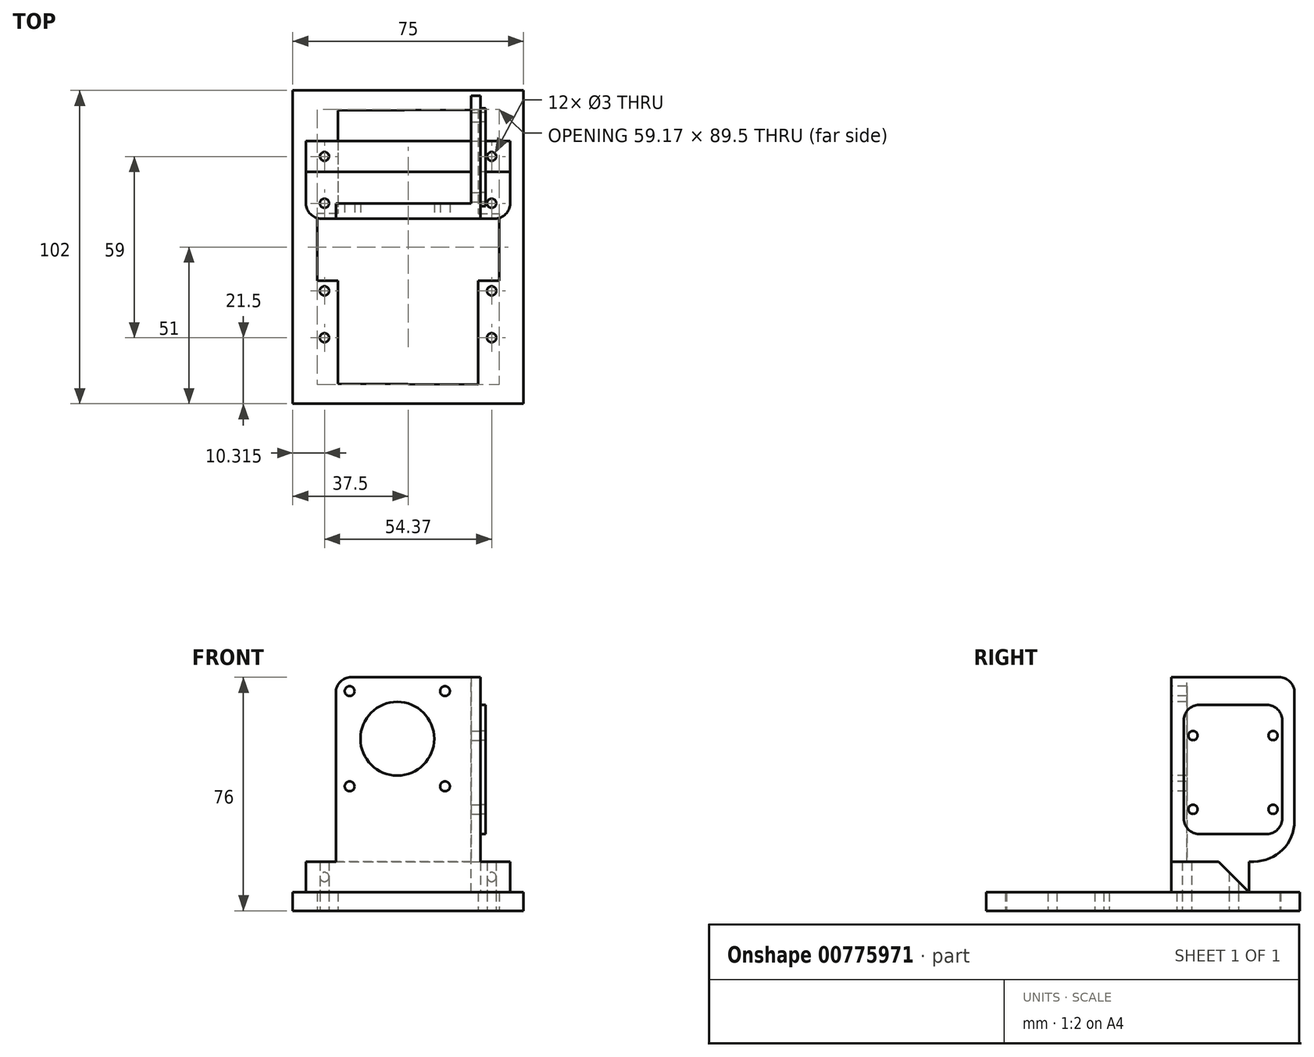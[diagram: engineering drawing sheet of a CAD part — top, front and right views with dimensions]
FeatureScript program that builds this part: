
annotation { "Feature Type Name" : "Feature", "Feature Type Description" : "" }
export const myFeature = defineFeature(function(context is Context, id is Id, definition is map)
    precondition{}
    {
        {
            var Q0;
            Q0=qCreatedBy(makeId("Top.planeOp"),FACE);
            var sketch = newSketch(context, id + "F0", { "sketchPlane" : qUnion([Q0])});
            skLineSegment(sketch, "E0.bottom", {"start": v(-22.79, 44.45) * mm, "end": v(22.79, 44.75) * mm});
            skPoint(sketch, "E0.middle", {"position": v(0, 0) * mm});
            skCircle(sketch, "E1", {"center": v(27.18, 29.5) * mm, "radius": 1.5 * mm});
            skCircle(sketch, "E2", {"center": v(27.18, 14.25) * mm, "radius": 1.5 * mm});
            skLineSegment(sketch, "E3", {"start": v(0, 44.6) * mm, "end": v(0, -44.6) * mm, "construction": true});
            skLineSegment(sketch, "E4", {"start": v(29.59, 0) * mm, "end": v(-29.59, 0) * mm, "construction": true});
            skLineSegment(sketch, "E5", {"start": v(27.18, 29.5) * mm, "end": v(27.18, 14.25) * mm});
            skCircle(sketch, "E6.MirrorC", {"center": v(-27.18, 29.5) * mm, "radius": 1.5 * mm});
            skCircle(sketch, "E7.MirrorC", {"center": v(-27.18, 14.25) * mm, "radius": 1.5 * mm});
            skCircle(sketch, "E8.MirrorC", {"center": v(-27.18, -14.25) * mm, "radius": 1.5 * mm});
            skCircle(sketch, "E9.MirrorC", {"center": v(-27.18, -29.5) * mm, "radius": 1.5 * mm});
            skCircle(sketch, "E10.MirrorC", {"center": v(27.18, -14.25) * mm, "radius": 1.5 * mm});
            skCircle(sketch, "E11.MirrorC", {"center": v(27.19, -29.5) * mm, "radius": 1.5 * mm});
            skLineSegment(sketch, "E12", {"start": v(22.78, 44.75) * mm, "end": v(22.78, 10.95) * mm});
            skLineSegment(sketch, "E13", {"start": v(22.79, 10.95) * mm, "end": v(29.59, 10.95) * mm});
            skLineSegment(sketch, "E14", {"start": v(-22.79, 44.45) * mm, "end": v(-22.79, 10.95) * mm});
            skLineSegment(sketch, "E15", {"start": v(-22.78, 10.95) * mm, "end": v(-29.58, 10.95) * mm});
            skLineSegment(sketch, "E16", {"start": v(-29.59, 10.95) * mm, "end": v(-29.59, 0) * mm});
            skLineSegment(sketch, "E17", {"start": v(29.59, 10.95) * mm, "end": v(29.59, 0) * mm});
            skLineSegment(sketch, "E18.MirrorCS", {"start": v(-29.59, -10.95) * mm, "end": v(-29.59, 0) * mm});
            skLineSegment(sketch, "E19.MirrorCS", {"start": v(-22.78, -10.95) * mm, "end": v(-29.58, -10.95) * mm});
            skLineSegment(sketch, "E20.MirrorCS", {"start": v(-22.78, -44.45) * mm, "end": v(-22.79, -10.95) * mm});
            skLineSegment(sketch, "E21.MirrorCS", {"start": v(22.79, -44.75) * mm, "end": v(22.79, -10.95) * mm});
            skLineSegment(sketch, "E22.MirrorCS", {"start": v(22.79, -10.95) * mm, "end": v(29.59, -10.95) * mm});
            skLineSegment(sketch, "E23.MirrorCS", {"start": v(29.59, -10.95) * mm, "end": v(29.59, 0) * mm});
            skLineSegment(sketch, "E24.MirrorCS", {"start": v(-22.79, -44.45) * mm, "end": v(22.79, -44.75) * mm});
            skLineSegment(sketch, "E25.bottom", {"start": v(37.5, 51) * mm, "end": v(-37.5, 51) * mm});
            skLineSegment(sketch, "E25.top", {"start": v(37.5, -51) * mm, "end": v(-37.5, -51) * mm});
            skLineSegment(sketch, "E25.left", {"start": v(37.5, 51) * mm, "end": v(37.5, -51) * mm});
            skLineSegment(sketch, "E25.right", {"start": v(-37.5, 51) * mm, "end": v(-37.5, -51) * mm});
            skSolve(sketch);
        }
        {
            var Q0;
            Q0=makeQuery(id+"F0.imprint","IMPRINT",FACE,{"disambiguationData":[TD([[makeQuery(id+"F0.imprint","IMPRINT",EDGE,{"derivedFrom":sQuery(id+"F0.wireOp",EDGE,"E0.bottom")}),1.0]])]});
            extrude(context, id + "F1", {"entities" : qUnion([Q0]), "depth" : 6 * mm, "offsetDistance" : 25 * mm});
        }
        {
            var Q0;
            Q0=makeQuery(id+"F1.opExtrude","CAP_FACE",FACE,{"disambiguationData":[OSD([sQuery(id+"F0.wireOp",EDGE,"E0.bottom"),sQuery(id+"F0.wireOp",EDGE,"E1"),sQuery(id+"F0.wireOp",EDGE,"E2"),sQuery(id+"F0.wireOp",EDGE,"E6.MirrorC"),sQuery(id+"F0.wireOp",EDGE,"E7.MirrorC"),sQuery(id+"F0.wireOp",EDGE,"E8.MirrorC"),sQuery(id+"F0.wireOp",EDGE,"E9.MirrorC"),sQuery(id+"F0.wireOp",EDGE,"E10.MirrorC"),sQuery(id+"F0.wireOp",EDGE,"E11.MirrorC"),sQuery(id+"F0.wireOp",EDGE,"E12"),sQuery(id+"F0.wireOp",EDGE,"E13"),sQuery(id+"F0.wireOp",EDGE,"E14"),sQuery(id+"F0.wireOp",EDGE,"E15"),sQuery(id+"F0.wireOp",EDGE,"E16"),sQuery(id+"F0.wireOp",EDGE,"E17"),sQuery(id+"F0.wireOp",EDGE,"E18.MirrorCS"),sQuery(id+"F0.wireOp",EDGE,"E19.MirrorCS"),sQuery(id+"F0.wireOp",EDGE,"E20.MirrorCS"),sQuery(id+"F0.wireOp",EDGE,"E21.MirrorCS"),sQuery(id+"F0.wireOp",EDGE,"E22.MirrorCS"),sQuery(id+"F0.wireOp",EDGE,"E23.MirrorCS"),sQuery(id+"F0.wireOp",EDGE,"E24.MirrorCS"),sQuery(id+"F0.wireOp",EDGE,"E25.bottom"),sQuery(id+"F0.wireOp",EDGE,"E25.top"),sQuery(id+"F0.wireOp",EDGE,"E25.left"),sQuery(id+"F0.wireOp",EDGE,"E25.right")])],"isStart":false});
            var sketch = newSketch(context, id + "F2", { "sketchPlane" : qUnion([Q0])});
            skLineSegment(sketch, "E26.bottom", {"start": v(-33.18, 34.5) * mm, "end": v(33.18, 34.5) * mm});
            skLineSegment(sketch, "E26.top", {"start": v(-33.18, 9.25) * mm, "end": v(33.18, 9.25) * mm});
            skLineSegment(sketch, "E26.left", {"start": v(-33.18, 34.5) * mm, "end": v(-33.18, 9.25) * mm});
            skLineSegment(sketch, "E26.right", {"start": v(33.18, 34.5) * mm, "end": v(33.18, 9.25) * mm});
            skCircle(sketch, "E27.0", {"center": v(-27.18, 29.5) * mm, "radius": 1.5 * mm});
            skCircle(sketch, "E28.0", {"center": v(-27.18, 14.25) * mm, "radius": 1.5 * mm});
            skCircle(sketch, "E29.0", {"center": v(27.18, 29.5) * mm, "radius": 1.5 * mm});
            skCircle(sketch, "E30.0", {"center": v(27.18, 14.25) * mm, "radius": 1.5 * mm});
            skPoint(sketch, "E31", {"position": v(0, 21.88) * mm});
            skPoint(sketch, "E32", {"position": v(-33.18, 34.5) * mm});
            skLineSegment(sketch, "E33", {"start": v(-27.18, 34.5) * mm, "end": v(-27.18, 29.5) * mm, "construction": true});
            skLineSegment(sketch, "E34", {"start": v(-27.18, 14.25) * mm, "end": v(-27.18, 9.25) * mm, "construction": true});
            skSolve(sketch);
        }
        {
            var Q0;
            {var subQ0=sQuery(id+"F2.wireOp",EDGE,"E26.left");Q0=makeQuery(id+"F2.imprint","IMPRINT",FACE,{"disambiguationData":[TD([[makeQuery(id+"F2.imprint","IMPRINT",EDGE,{"derivedFrom":subQ0}),1.0]])]});}
            var Q1;
            {var subQ1=makeQuery(id+"F1.opExtrude","CAP_EDGE",EDGE,{"disambiguationData":[OSD([sQuery(id+"F0.wireOp",EDGE,"E13")])],"isStart":false});Q1=makeQuery(id+"F2.imprint","IMPRINT",FACE,{"disambiguationData":[TD([[makeQuery(id+"F2.imprint","IMPRINT",EDGE,{"derivedFrom":subQ1}),-1.0]])]});}
            var Q2;
            {var subQ0=sQuery(id+"F2.wireOp",EDGE,"E26.right");Q2=makeQuery(id+"F2.imprint","IMPRINT",FACE,{"disambiguationData":[TD([[makeQuery(id+"F2.imprint","IMPRINT",EDGE,{"derivedFrom":subQ0}),-1.0]])]});}
            extrude(context, id + "F3", {"entities" : qUnion([Q0, Q1, Q2]), "depth" : 10 * mm, "offsetDistance" : 25 * mm});
        }
        {
            var Q0;
            Q0=makeQuery(id+"F3.opExtrude","CAP_FACE",FACE,{"disambiguationData":[OSD([sQuery(id+"F2.wireOp",EDGE,"E26.bottom"),sQuery(id+"F2.wireOp",EDGE,"E26.top"),sQuery(id+"F2.wireOp",EDGE,"E26.left"),sQuery(id+"F2.wireOp",EDGE,"E26.right"),sQuery(id+"F2.wireOp",EDGE,"E27.0"),sQuery(id+"F2.wireOp",EDGE,"E28.0"),sQuery(id+"F2.wireOp",EDGE,"E29.0"),sQuery(id+"F2.wireOp",EDGE,"E30.0")])],"isStart":false});
            var sketch = newSketch(context, id + "F4", { "sketchPlane" : qUnion([Q0])});
            skLineSegment(sketch, "E35", {"start": v(-23.5, 9.25) * mm, "end": v(-23.5, 14.25) * mm});
            skLineSegment(sketch, "E36", {"start": v(-23.5, 14.25) * mm, "end": v(23.5, 14.25) * mm});
            skLineSegment(sketch, "E37", {"start": v(23.5, 14.25) * mm, "end": v(23.5, 9.25) * mm});
            skPoint(sketch, "E38", {"position": v(0, 11.75) * mm});
            skSolve(sketch);
        }
        {
            var Q0;
            {var subQ0=sQuery(id+"F4.wireOp",EDGE,"E35");Q0=makeQuery(id+"F4.imprint","IMPRINT",FACE,{"disambiguationData":[TD([[makeQuery(id+"F4.imprint","IMPRINT",EDGE,{"derivedFrom":subQ0}),-1.0]])]});}
            extrude(context, id + "F5", {"entities" : qUnion([Q0]), "operationType" : NewBodyOperationType.ADD, "depth" : 60 * mm, "offsetDistance" : 25 * mm});
        }
        {
            var Q0;
            {var subQ0=sQuery(id+"F2.wireOp",EDGE,"E26.top");Q0=makeQuery(id+"F5.boolean.opBoolean","MERGE",FACE,{"derivedFrom":[makeQuery(id+"F3.opExtrude","SWEPT_FACE",FACE,{"disambiguationData":[OSD([subQ0])]}),makeQuery(id+"F5.opExtrude","SWEPT_FACE",FACE,{"disambiguationData":[OSD([subQ0])]})]});}
            var sketch = newSketch(context, id + "F6", { "sketchPlane" : qUnion([Q0])});
            skPoint(sketch, "E39", {"position": v(-3.5, 56) * mm});
            skCircle(sketch, "E40", {"center": v(-3.5, 56) * mm, "radius": 12 * mm});
            skCircle(sketch, "E41", {"center": v(-19, 71.5) * mm, "radius": 1.6 * mm});
            skCircle(sketch, "E42.1.0", {"center": v(-19, 40.5) * mm, "radius": 1.6 * mm});
            skCircle(sketch, "E42.2.0", {"center": v(12, 40.5) * mm, "radius": 1.6 * mm});
            skCircle(sketch, "E42.3.0", {"center": v(12, 71.5) * mm, "radius": 1.6 * mm});
            skLineSegment(sketch, "E43", {"start": v(20.5, 76) * mm, "end": v(20.5, 16) * mm});
            skLineSegment(sketch, "E44", {"start": v(20.5, 16) * mm, "end": v(23.5, 16) * mm});
            skSolve(sketch);
        }
        {
            var Q0;
            Q0=makeQuery(id+"F6.imprint","IMPRINT",FACE,{"disambiguationData":[TD([[makeQuery(id+"F6.imprint","IMPRINT",EDGE,{"derivedFrom":sQuery(id+"F6.wireOp",EDGE,"E40")}),1.0]])]});
            var Q1;
            Q1=makeQuery(id+"F6.imprint","IMPRINT",FACE,{"disambiguationData":[TD([[makeQuery(id+"F6.imprint","IMPRINT",EDGE,{"derivedFrom":sQuery(id+"F6.wireOp",EDGE,"E41")}),1.0]])]});
            var Q2;
            Q2=makeQuery(id+"F6.imprint","IMPRINT",FACE,{"disambiguationData":[TD([[makeQuery(id+"F6.imprint","IMPRINT",EDGE,{"derivedFrom":sQuery(id+"F6.wireOp",EDGE,"E42.3.0")}),1.0]])]});
            var Q3;
            Q3=makeQuery(id+"F6.imprint","IMPRINT",FACE,{"disambiguationData":[TD([[makeQuery(id+"F6.imprint","IMPRINT",EDGE,{"derivedFrom":sQuery(id+"F6.wireOp",EDGE,"E42.2.0")}),1.0]])]});
            var Q4;
            Q4=makeQuery(id+"F6.imprint","IMPRINT",FACE,{"disambiguationData":[TD([[makeQuery(id+"F6.imprint","IMPRINT",EDGE,{"derivedFrom":sQuery(id+"F6.wireOp",EDGE,"E42.1.0")}),1.0]])]});
            extrude(context, id + "F7", {"entities" : qUnion([Q0, Q1, Q2, Q3, Q4]), "operationType" : NewBodyOperationType.REMOVE, "oppositeDirection" : true, "depth" : 25 * mm, "offsetDistance" : 25 * mm});
        }
        {
            var Q0;
            {var subQ0=sQuery(id+"F6.wireOp",EDGE,"E43");Q0=makeQuery(id+"F6.imprint","IMPRINT",FACE,{"disambiguationData":[TD([[makeQuery(id+"F6.imprint","IMPRINT",EDGE,{"derivedFrom":subQ0}),1.0]])]});}
            extrude(context, id + "F8", {"entities" : qUnion([Q0]), "operationType" : NewBodyOperationType.ADD, "oppositeDirection" : true, "depth" : 40 * mm, "offsetDistance" : 25 * mm});
        }
        {
            var Q0;
            {var subQ0=sQuery(id+"F4.wireOp",EDGE,"E37");Q0=makeQuery(id+"F8.boolean.opBoolean","MERGE",FACE,{"derivedFrom":[makeQuery(id+"F5.opExtrude","SWEPT_FACE",FACE,{"disambiguationData":[OSD([subQ0])]}),makeQuery(id+"F8.opExtrude","SWEPT_FACE",FACE,{"disambiguationData":[OSD([sQuery(id+"F2.wireOp",EDGE,"E26.top"),subQ0])]})]});}
            var sketch = newSketch(context, id + "F9", { "sketchPlane" : qUnion([Q0])});
            skPoint(sketch, "E45", {"position": v(29.25, 46) * mm});
            skLineSegment(sketch, "E46.bottom", {"start": v(18.25, 67) * mm, "end": v(40.25, 67) * mm});
            skLineSegment(sketch, "E46.top", {"start": v(18.25, 25) * mm, "end": v(40.25, 25) * mm});
            skLineSegment(sketch, "E46.left", {"start": v(13.25, 62) * mm, "end": v(13.25, 30) * mm});
            skLineSegment(sketch, "E46.right", {"start": v(45.25, 62) * mm, "end": v(45.25, 30) * mm});
            skCircle(sketch, "E47", {"center": v(16.25, 57) * mm, "radius": 1.5 * mm});
            skCircle(sketch, "E48", {"center": v(16.25, 33) * mm, "radius": 1.5 * mm});
            skCircle(sketch, "E49", {"center": v(42.25, 33) * mm, "radius": 1.5 * mm});
            skCircle(sketch, "E50", {"center": v(42.25, 57) * mm, "radius": 1.5 * mm});
            skPoint(sketch, "E51.visualSharp", {"position": v(13.25, 67) * mm});
            skArc(sketch, "E51.filletArc", {"start": v(18.25, 67) * mm, "mid": v(14.71, 65.54) * mm, "end": v(13.25, 62) * mm});
            skPoint(sketch, "E52.visualSharp", {"position": v(45.25, 67) * mm});
            skArc(sketch, "E52.filletArc", {"start": v(45.25, 62) * mm, "mid": v(43.79, 65.54) * mm, "end": v(40.25, 67) * mm});
            skPoint(sketch, "E53.visualSharp", {"position": v(45.25, 25) * mm});
            skArc(sketch, "E53.filletArc", {"start": v(40.25, 25) * mm, "mid": v(43.79, 26.46) * mm, "end": v(45.25, 30) * mm});
            skPoint(sketch, "E54.visualSharp", {"position": v(13.25, 25) * mm});
            skArc(sketch, "E54.filletArc", {"start": v(13.25, 30) * mm, "mid": v(14.71, 26.46) * mm, "end": v(18.25, 25) * mm});
            skSolve(sketch);
        }
        {
            var Q0;
            Q0=makeQuery(id+"F9.imprint","IMPRINT",FACE,{"disambiguationData":[TD([[makeQuery(id+"F9.imprint","IMPRINT",EDGE,{"derivedFrom":sQuery(id+"F9.wireOp",EDGE,"E47")}),1.0]])]});
            var Q1;
            Q1=makeQuery(id+"F9.imprint","IMPRINT",FACE,{"disambiguationData":[TD([[makeQuery(id+"F9.imprint","IMPRINT",EDGE,{"derivedFrom":sQuery(id+"F9.wireOp",EDGE,"E50")}),1.0]])]});
            var Q2;
            Q2=makeQuery(id+"F9.imprint","IMPRINT",FACE,{"disambiguationData":[TD([[makeQuery(id+"F9.imprint","IMPRINT",EDGE,{"derivedFrom":sQuery(id+"F9.wireOp",EDGE,"E48")}),1.0]])]});
            var Q3;
            Q3=makeQuery(id+"F9.imprint","IMPRINT",FACE,{"disambiguationData":[TD([[makeQuery(id+"F9.imprint","IMPRINT",EDGE,{"derivedFrom":sQuery(id+"F9.wireOp",EDGE,"E49")}),1.0]])]});
            extrude(context, id + "F10", {"entities" : qUnion([Q0, Q1, Q2, Q3]), "operationType" : NewBodyOperationType.REMOVE, "oppositeDirection" : true, "depth" : 25 * mm, "offsetDistance" : 25 * mm});
        }
        {
            var Q0;
            {var subQ0=sQuery(id+"F2.wireOp",EDGE,"E26.bottom");Q0=makeQuery(id+"F8.boolean.opBoolean","SPLIT",EDGE,{"disambiguationData":[topologyDisambiguationEdgeConnected([makeQuery(id+"F3.opExtrude","SWEPT_FACE",FACE,{"disambiguationData":[OSD([subQ0])]}),makeQuery(id+"F8.opExtrude","SWEPT_FACE",FACE,{"disambiguationData":[OSD([sQuery(id+"F6.wireOp",EDGE,"E44")])]})])],"derivedFrom":makeQuery(id+"F3.opExtrude","CAP_EDGE",EDGE,{"disambiguationData":[OSD([subQ0])],"isStart":false})});}
            chamfer(context, id + "F11", {"entities" : qUnion([Q0]), "width" : 10 * mm, "tangentPropagation" : true});
        }
        {
            var Q0;
            Q0=makeQuery(id+"F8.opExtrude","CAP_EDGE",EDGE,{"disambiguationData":[OSD([sQuery(id+"F6.wireOp",EDGE,"E44")])],"isStart":false});
            fillet(context, id + "F12", {"entities" : qUnion([Q0]), "radius" : 13.28 * mm, "tangentPropagation" : true, "allowEdgeOverflow" : false});
        }
        {
            var Q0;
            Q0=makeQuery(id+"F9.imprint","IMPRINT",FACE,{"disambiguationData":[TD([[makeQuery(id+"F9.imprint","IMPRINT",EDGE,{"derivedFrom":sQuery(id+"F9.wireOp",EDGE,"E46.bottom")}),-1.0]])]});
            extrude(context, id + "F13", {"entities" : qUnion([Q0]), "depth" : 1.7 * mm, "offsetDistance" : 25 * mm});
        }
        {
            var Q0;
            Q0=makeQuery(id+"F8.opExtrude","CAP_EDGE",EDGE,{"disambiguationData":[OSD([sQuery(id+"F2.wireOp",EDGE,"E26.top")])],"isStart":false});
            var Q1;
            Q1=makeQuery(id+"F5.opExtrude","CAP_EDGE",EDGE,{"disambiguationData":[OSD([sQuery(id+"F4.wireOp",EDGE,"E35")])],"isStart":false});
            var Q2;
            Q2=makeQuery(id+"F3.opExtrude","SWEPT_EDGE",EDGE,{"disambiguationData":[OSD([sQuery(id+"F2.wireOp",EDGE,"E26.bottom"),sQuery(id+"F2.wireOp",EDGE,"E26.left")])]});
            var Q3;
            Q3=makeQuery(id+"F3.opExtrude","SWEPT_EDGE",EDGE,{"disambiguationData":[OSD([sQuery(id+"F2.wireOp",EDGE,"E26.top"),sQuery(id+"F2.wireOp",EDGE,"E26.left")])]});
            var Q4;
            Q4=makeQuery(id+"F3.opExtrude","SWEPT_EDGE",EDGE,{"disambiguationData":[OSD([sQuery(id+"F2.wireOp",EDGE,"E26.top"),sQuery(id+"F2.wireOp",EDGE,"E26.right")])]});
            var Q5;
            Q5=makeQuery(id+"F3.opExtrude","SWEPT_EDGE",EDGE,{"disambiguationData":[OSD([sQuery(id+"F2.wireOp",EDGE,"E26.bottom"),sQuery(id+"F2.wireOp",EDGE,"E26.right")])]});
            fillet(context, id + "F14", {"entities" : qUnion([Q0, Q1, Q2, Q3, Q4, Q5]), "radius" : 5 * mm, "tangentPropagation" : true, "allowEdgeOverflow" : false});
        }
    });
